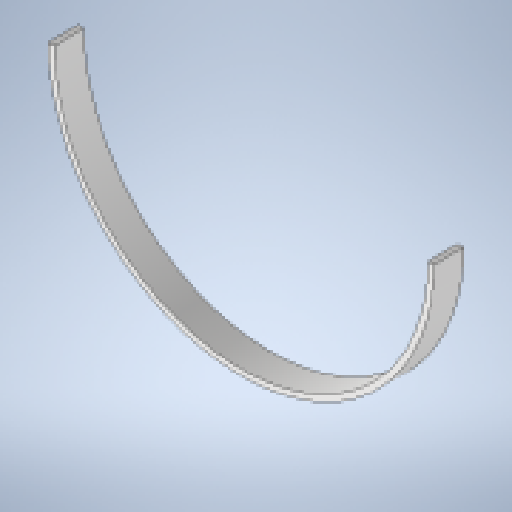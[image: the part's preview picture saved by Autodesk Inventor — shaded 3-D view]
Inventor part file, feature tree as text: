
AUTODESK INVENTOR PART (.ipt)
format: ipt  version: 2025 (Build 290162010, 162A)  size: 162,304 bytes
history: native  units: mm
features: sheet_metal_op x3, sketch x1, other x1
ambient origin geometry x8: Origin, YZ Plane, XZ Plane, XY Plane, X Axis, Y Axis, Z Axis, Center Point
bodies: Body1 (feature_tree)
feature tree (5):
  sheet_metal_op  "Contour Flange1"
  sketch  "Sketch8"  dims[d46=330.0mm d47=6.0mm d48=6.0mm d49=3.0mm d50=12.0mm d51=6.0mm d52=30.0mm d53=6.0mm d54=6.0mm d55=24.0mm d56=6.0mm d57=6.0mm]
  other  "Plate1"
  sheet_metal_op  "Bend1"
  sheet_metal_op  "Corner1"
